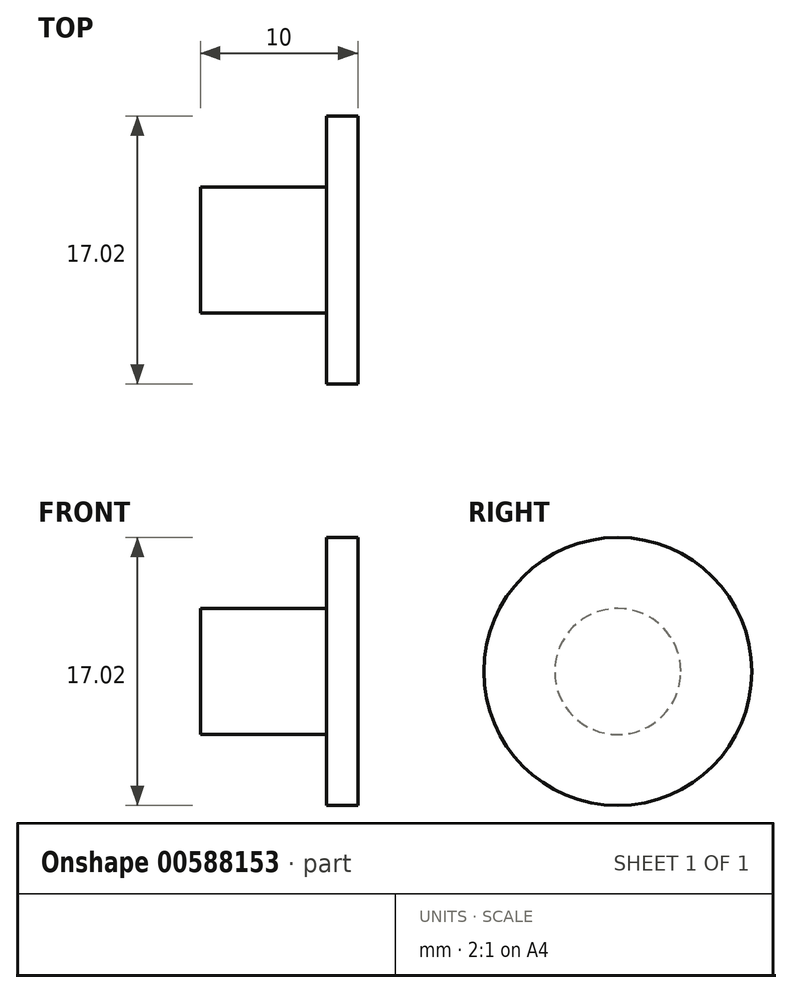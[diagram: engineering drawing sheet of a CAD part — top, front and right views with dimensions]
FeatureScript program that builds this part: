
annotation { "Feature Type Name" : "Feature", "Feature Type Description" : "" }
export const myFeature = defineFeature(function(context is Context, id is Id, definition is map)
    precondition{}
    {
        {
            var Q0;
            Q0=qCreatedBy(makeId("Right.planeOp"),FACE);
            var sketch = newSketch(context, id + "F0", { "sketchPlane" : qUnion([Q0])});
            skCircle(sketch, "E0", {"center": v(0, 0) * mm, "radius": 4 * mm});
            skSolve(sketch);
        }
        {
            var Q0;
            Q0=makeQuery(id+"F0.imprint","IMPRINT",FACE,{"disambiguationData":[TD([[makeQuery(id+"F0.imprint","IMPRINT",EDGE,{"derivedFrom":sQuery(id+"F0.wireOp",EDGE,"E0")}),1.0]])]});
            extrude(context, id + "F1", {"entities" : qUnion([Q0]), "depth" : 8 * mm, "offsetDistance" : 25.4 * mm});
        }
        {
            var Q0;
            Q0=makeQuery(id+"F1.opExtrude","CAP_FACE",FACE,{"disambiguationData":[OSD([sQuery(id+"F0.wireOp",EDGE,"E0")])],"isStart":false});
            var sketch = newSketch(context, id + "F2", { "sketchPlane" : qUnion([Q0])});
            skCircle(sketch, "E1", {"center": v(0, 0) * mm, "radius": 8.51 * mm});
            skSolve(sketch);
        }
        {
            var Q0;
            Q0 = qSketchRegion(id + "F2", true);
            extrude(context, id + "F3", {"entities" : qUnion([Q0]), "operationType" : NewBodyOperationType.ADD, "depth" : 2 * mm, "offsetDistance" : 25.4 * mm});
        }
    });
